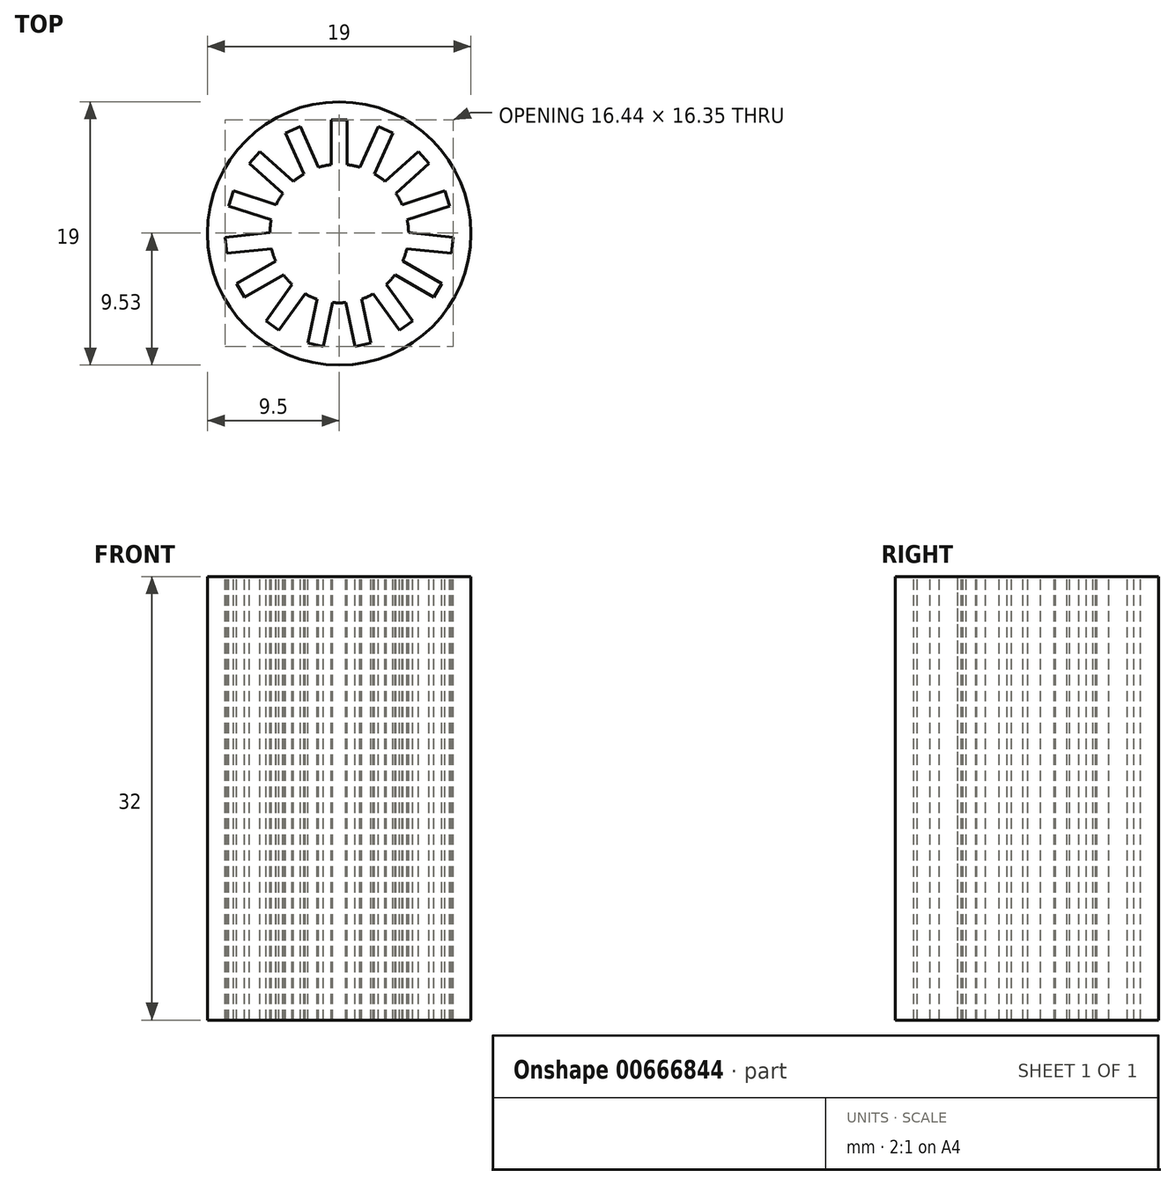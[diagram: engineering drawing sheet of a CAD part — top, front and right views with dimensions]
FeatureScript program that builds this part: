
annotation { "Feature Type Name" : "Feature", "Feature Type Description" : "" }
export const myFeature = defineFeature(function(context is Context, id is Id, definition is map)
    precondition{}
    {
        {
            var Q0;
            Q0=qCreatedBy(makeId("Top.planeOp"),FACE);
            var sketch = newSketch(context, id + "F0", { "sketchPlane" : qUnion([Q0])});
            skCircle(sketch, "E0", {"center": v(0, 0) * mm, "radius": 9.5 * mm});
            skCircle(sketch, "E1", {"center": v(0, 0) * mm, "radius": 5 * mm});
            skSolve(sketch);
        }
        {
            var Q0;
            Q0 = qSketchRegion(id + "F0", true);
            extrude(context, id + "F1", {"entities" : qUnion([Q0]), "depth" : 32 * mm, "offsetDistance" : 25 * mm});
        }
        {
            var Q0;
            Q0=makeQuery(id+"F1.opExtrude","CAP_FACE",FACE,{"disambiguationData":[OSD([sQuery(id+"F0.wireOp",EDGE,"E0"),sQuery(id+"F0.wireOp",EDGE,"E1")])],"isStart":false});
            var sketch = newSketch(context, id + "F2", { "sketchPlane" : qUnion([Q0])});
            skLineSegment(sketch, "E2.bottom", {"start": v(0.58, 8.2) * mm, "end": v(-0.58, 8.2) * mm});
            skLineSegment(sketch, "E2.top", {"start": v(0.58, 1.8) * mm, "end": v(-0.58, 1.8) * mm});
            skLineSegment(sketch, "E2.left", {"start": v(0.58, 8.2) * mm, "end": v(0.58, 1.8) * mm});
            skLineSegment(sketch, "E2.right", {"start": v(-0.58, 8.2) * mm, "end": v(-0.58, 1.8) * mm});
            skPoint(sketch, "E2.middle", {"position": v(0, 5) * mm});
            skLineSegment(sketch, "E3.1.0", {"start": v(-0.2, 1.88) * mm, "end": v(-1.26, 1.4) * mm});
            skLineSegment(sketch, "E3.1.1", {"start": v(-3.86, 7.26) * mm, "end": v(-1.26, 1.4) * mm});
            skLineSegment(sketch, "E3.1.2", {"start": v(-2.8, 7.73) * mm, "end": v(-3.86, 7.26) * mm});
            skPoint(sketch, "E3.1.3", {"position": v(-2.03, 4.57) * mm});
            skLineSegment(sketch, "E3.1.4", {"start": v(-2.8, 7.73) * mm, "end": v(-0.2, 1.88) * mm});
            skLineSegment(sketch, "E3.2.0", {"start": v(-0.95, 1.63) * mm, "end": v(-1.72, 0.77) * mm});
            skLineSegment(sketch, "E3.2.1", {"start": v(-6.48, 5.06) * mm, "end": v(-1.72, 0.77) * mm});
            skLineSegment(sketch, "E3.2.2", {"start": v(-5.7, 5.92) * mm, "end": v(-6.48, 5.06) * mm});
            skPoint(sketch, "E3.2.3", {"position": v(-3.72, 3.35) * mm});
            skLineSegment(sketch, "E3.2.4", {"start": v(-5.7, 5.92) * mm, "end": v(-0.95, 1.63) * mm});
            skLineSegment(sketch, "E3.3.0", {"start": v(-1.53, 1.1) * mm, "end": v(-1.89, 0) * mm});
            skLineSegment(sketch, "E3.3.1", {"start": v(-7.98, 1.98) * mm, "end": v(-1.89, 0) * mm});
            skLineSegment(sketch, "E3.3.2", {"start": v(-7.62, 3.08) * mm, "end": v(-7.98, 1.98) * mm});
            skPoint(sketch, "E3.3.3", {"position": v(-4.76, 1.55) * mm});
            skLineSegment(sketch, "E3.3.4", {"start": v(-7.62, 3.08) * mm, "end": v(-1.53, 1.1) * mm});
            skLineSegment(sketch, "E3.4.0", {"start": v(-1.85, 0.39) * mm, "end": v(-1.73, -0.76) * mm});
            skLineSegment(sketch, "E3.4.1", {"start": v(-8.1, -1.43) * mm, "end": v(-1.73, -0.76) * mm});
            skLineSegment(sketch, "E3.4.2", {"start": v(-8.22, -0.28) * mm, "end": v(-8.1, -1.43) * mm});
            skPoint(sketch, "E3.4.3", {"position": v(-4.97, -0.52) * mm});
            skLineSegment(sketch, "E3.4.4", {"start": v(-8.22, -0.28) * mm, "end": v(-1.85, 0.39) * mm});
            skLineSegment(sketch, "E3.5.0", {"start": v(-1.85, -0.4) * mm, "end": v(-1.27, -1.4) * mm});
            skLineSegment(sketch, "E3.5.1", {"start": v(-6.81, -4.6) * mm, "end": v(-1.27, -1.4) * mm});
            skLineSegment(sketch, "E3.5.2", {"start": v(-7.4, -3.6) * mm, "end": v(-6.81, -4.6) * mm});
            skPoint(sketch, "E3.5.3", {"position": v(-4.33, -2.5) * mm});
            skLineSegment(sketch, "E3.5.4", {"start": v(-7.4, -3.6) * mm, "end": v(-1.85, -0.4) * mm});
            skLineSegment(sketch, "E3.6.0", {"start": v(-1.52, -1.11) * mm, "end": v(-0.59, -1.8) * mm});
            skLineSegment(sketch, "E3.6.1", {"start": v(-4.35, -6.98) * mm, "end": v(-0.59, -1.8) * mm});
            skLineSegment(sketch, "E3.6.2", {"start": v(-5.29, -6.3) * mm, "end": v(-4.35, -6.98) * mm});
            skPoint(sketch, "E3.6.3", {"position": v(-2.94, -4.05) * mm});
            skLineSegment(sketch, "E3.6.4", {"start": v(-5.29, -6.3) * mm, "end": v(-1.52, -1.11) * mm});
            skLineSegment(sketch, "E3.7.0", {"start": v(-0.94, -1.64) * mm, "end": v(0.2, -1.88) * mm});
            skLineSegment(sketch, "E3.7.1", {"start": v(-1.14, -8.14) * mm, "end": v(0.2, -1.88) * mm});
            skLineSegment(sketch, "E3.7.2", {"start": v(-2.27, -7.9) * mm, "end": v(-1.14, -8.14) * mm});
            skPoint(sketch, "E3.7.3", {"position": v(-1.04, -4.9) * mm});
            skLineSegment(sketch, "E3.7.4", {"start": v(-2.27, -7.9) * mm, "end": v(-0.94, -1.64) * mm});
            skLineSegment(sketch, "E3.8.0", {"start": v(-0.2, -1.88) * mm, "end": v(0.94, -1.64) * mm});
            skLineSegment(sketch, "E3.8.1", {"start": v(2.27, -7.9) * mm, "end": v(0.94, -1.64) * mm});
            skLineSegment(sketch, "E3.8.2", {"start": v(1.14, -8.14) * mm, "end": v(2.27, -7.9) * mm});
            skPoint(sketch, "E3.8.3", {"position": v(1.04, -4.9) * mm});
            skLineSegment(sketch, "E3.8.4", {"start": v(1.14, -8.14) * mm, "end": v(-0.2, -1.88) * mm});
            skLineSegment(sketch, "E3.9.0", {"start": v(0.59, -1.8) * mm, "end": v(1.52, -1.11) * mm});
            skLineSegment(sketch, "E3.9.1", {"start": v(5.29, -6.3) * mm, "end": v(1.52, -1.11) * mm});
            skLineSegment(sketch, "E3.9.2", {"start": v(4.35, -6.98) * mm, "end": v(5.29, -6.3) * mm});
            skPoint(sketch, "E3.9.3", {"position": v(2.94, -4.05) * mm});
            skLineSegment(sketch, "E3.9.4", {"start": v(4.35, -6.98) * mm, "end": v(0.59, -1.8) * mm});
            skLineSegment(sketch, "E3.10.0", {"start": v(1.27, -1.4) * mm, "end": v(1.85, -0.4) * mm});
            skLineSegment(sketch, "E3.10.1", {"start": v(7.4, -3.6) * mm, "end": v(1.85, -0.4) * mm});
            skLineSegment(sketch, "E3.10.2", {"start": v(6.81, -4.6) * mm, "end": v(7.4, -3.6) * mm});
            skPoint(sketch, "E3.10.3", {"position": v(4.33, -2.5) * mm});
            skLineSegment(sketch, "E3.10.4", {"start": v(6.81, -4.6) * mm, "end": v(1.27, -1.4) * mm});
            skLineSegment(sketch, "E3.11.0", {"start": v(1.73, -0.76) * mm, "end": v(1.85, 0.39) * mm});
            skLineSegment(sketch, "E3.11.1", {"start": v(8.22, -0.28) * mm, "end": v(1.85, 0.39) * mm});
            skLineSegment(sketch, "E3.11.2", {"start": v(8.1, -1.43) * mm, "end": v(8.22, -0.28) * mm});
            skPoint(sketch, "E3.11.3", {"position": v(4.97, -0.52) * mm});
            skLineSegment(sketch, "E3.11.4", {"start": v(8.1, -1.43) * mm, "end": v(1.73, -0.76) * mm});
            skLineSegment(sketch, "E3.12.0", {"start": v(1.89, 0) * mm, "end": v(1.53, 1.1) * mm});
            skLineSegment(sketch, "E3.12.1", {"start": v(7.62, 3.08) * mm, "end": v(1.53, 1.1) * mm});
            skLineSegment(sketch, "E3.12.2", {"start": v(7.98, 1.98) * mm, "end": v(7.62, 3.08) * mm});
            skPoint(sketch, "E3.12.3", {"position": v(4.76, 1.55) * mm});
            skLineSegment(sketch, "E3.12.4", {"start": v(7.98, 1.98) * mm, "end": v(1.89, 0) * mm});
            skLineSegment(sketch, "E3.13.0", {"start": v(1.72, 0.77) * mm, "end": v(0.95, 1.63) * mm});
            skLineSegment(sketch, "E3.13.1", {"start": v(5.7, 5.92) * mm, "end": v(0.95, 1.63) * mm});
            skLineSegment(sketch, "E3.13.2", {"start": v(6.48, 5.06) * mm, "end": v(5.7, 5.92) * mm});
            skPoint(sketch, "E3.13.3", {"position": v(3.72, 3.35) * mm});
            skLineSegment(sketch, "E3.13.4", {"start": v(6.48, 5.06) * mm, "end": v(1.72, 0.77) * mm});
            skLineSegment(sketch, "E3.14.0", {"start": v(1.26, 1.4) * mm, "end": v(0.2, 1.88) * mm});
            skLineSegment(sketch, "E3.14.1", {"start": v(2.8, 7.73) * mm, "end": v(0.2, 1.88) * mm});
            skLineSegment(sketch, "E3.14.2", {"start": v(3.86, 7.26) * mm, "end": v(2.8, 7.73) * mm});
            skPoint(sketch, "E3.14.3", {"position": v(2.03, 4.57) * mm});
            skLineSegment(sketch, "E3.14.4", {"start": v(3.86, 7.26) * mm, "end": v(1.26, 1.4) * mm});
            skPoint(sketch, "E3.center", {"position": v(0, 0) * mm});
            skSolve(sketch);
        }
        {
            var Q0;
            {var subQ0=sQuery(id+"F2.wireOp",EDGE,"E2.bottom");Q0=makeQuery(id+"F2.imprint","IMPRINT",FACE,{"disambiguationData":[TD([[makeQuery(id+"F2.imprint","IMPRINT",EDGE,{"derivedFrom":subQ0}),1.0]])]});}
            var Q1;
            {var subQ0=sQuery(id+"F2.wireOp",EDGE,"E3.1.2");Q1=makeQuery(id+"F2.imprint","IMPRINT",FACE,{"disambiguationData":[TD([[makeQuery(id+"F2.imprint","IMPRINT",EDGE,{"derivedFrom":subQ0}),1.0]])]});}
            var Q2;
            {var subQ0=sQuery(id+"F2.wireOp",EDGE,"E3.2.2");Q2=makeQuery(id+"F2.imprint","IMPRINT",FACE,{"disambiguationData":[TD([[makeQuery(id+"F2.imprint","IMPRINT",EDGE,{"derivedFrom":subQ0}),1.0]])]});}
            var Q3;
            {var subQ0=sQuery(id+"F2.wireOp",EDGE,"E3.3.2");Q3=makeQuery(id+"F2.imprint","IMPRINT",FACE,{"disambiguationData":[TD([[makeQuery(id+"F2.imprint","IMPRINT",EDGE,{"derivedFrom":subQ0}),1.0]])]});}
            var Q4;
            {var subQ0=sQuery(id+"F2.wireOp",EDGE,"E3.4.2");Q4=makeQuery(id+"F2.imprint","IMPRINT",FACE,{"disambiguationData":[TD([[makeQuery(id+"F2.imprint","IMPRINT",EDGE,{"derivedFrom":subQ0}),1.0]])]});}
            var Q5;
            {var subQ0=sQuery(id+"F2.wireOp",EDGE,"E3.5.2");Q5=makeQuery(id+"F2.imprint","IMPRINT",FACE,{"disambiguationData":[TD([[makeQuery(id+"F2.imprint","IMPRINT",EDGE,{"derivedFrom":subQ0}),1.0]])]});}
            var Q6;
            {var subQ0=sQuery(id+"F2.wireOp",EDGE,"E3.6.2");Q6=makeQuery(id+"F2.imprint","IMPRINT",FACE,{"disambiguationData":[TD([[makeQuery(id+"F2.imprint","IMPRINT",EDGE,{"derivedFrom":subQ0}),1.0]])]});}
            var Q7;
            {var subQ0=sQuery(id+"F2.wireOp",EDGE,"E3.7.2");Q7=makeQuery(id+"F2.imprint","IMPRINT",FACE,{"disambiguationData":[TD([[makeQuery(id+"F2.imprint","IMPRINT",EDGE,{"derivedFrom":subQ0}),1.0]])]});}
            var Q8;
            {var subQ0=sQuery(id+"F2.wireOp",EDGE,"E3.8.2");Q8=makeQuery(id+"F2.imprint","IMPRINT",FACE,{"disambiguationData":[TD([[makeQuery(id+"F2.imprint","IMPRINT",EDGE,{"derivedFrom":subQ0}),1.0]])]});}
            var Q9;
            {var subQ0=sQuery(id+"F2.wireOp",EDGE,"E3.9.2");Q9=makeQuery(id+"F2.imprint","IMPRINT",FACE,{"disambiguationData":[TD([[makeQuery(id+"F2.imprint","IMPRINT",EDGE,{"derivedFrom":subQ0}),1.0]])]});}
            var Q10;
            {var subQ0=sQuery(id+"F2.wireOp",EDGE,"E3.10.2");Q10=makeQuery(id+"F2.imprint","IMPRINT",FACE,{"disambiguationData":[TD([[makeQuery(id+"F2.imprint","IMPRINT",EDGE,{"derivedFrom":subQ0}),1.0]])]});}
            var Q11;
            {var subQ0=sQuery(id+"F2.wireOp",EDGE,"E3.11.2");Q11=makeQuery(id+"F2.imprint","IMPRINT",FACE,{"disambiguationData":[TD([[makeQuery(id+"F2.imprint","IMPRINT",EDGE,{"derivedFrom":subQ0}),1.0]])]});}
            var Q12;
            {var subQ0=sQuery(id+"F2.wireOp",EDGE,"E3.12.2");Q12=makeQuery(id+"F2.imprint","IMPRINT",FACE,{"disambiguationData":[TD([[makeQuery(id+"F2.imprint","IMPRINT",EDGE,{"derivedFrom":subQ0}),1.0]])]});}
            var Q13;
            {var subQ0=sQuery(id+"F2.wireOp",EDGE,"E3.13.2");Q13=makeQuery(id+"F2.imprint","IMPRINT",FACE,{"disambiguationData":[TD([[makeQuery(id+"F2.imprint","IMPRINT",EDGE,{"derivedFrom":subQ0}),1.0]])]});}
            var Q14;
            {var subQ0=sQuery(id+"F2.wireOp",EDGE,"E3.14.2");Q14=makeQuery(id+"F2.imprint","IMPRINT",FACE,{"disambiguationData":[TD([[makeQuery(id+"F2.imprint","IMPRINT",EDGE,{"derivedFrom":subQ0}),1.0]])]});}
            extrude(context, id + "F3", {"entities" : qUnion([Q0, Q1, Q2, Q3, Q4, Q5, Q6, Q7, Q8, Q9, Q10, Q11, Q12, Q13, Q14]), "operationType" : NewBodyOperationType.REMOVE, "oppositeDirection" : true, "depth" : 52 * mm, "offsetDistance" : 25 * mm});
        }
    });
